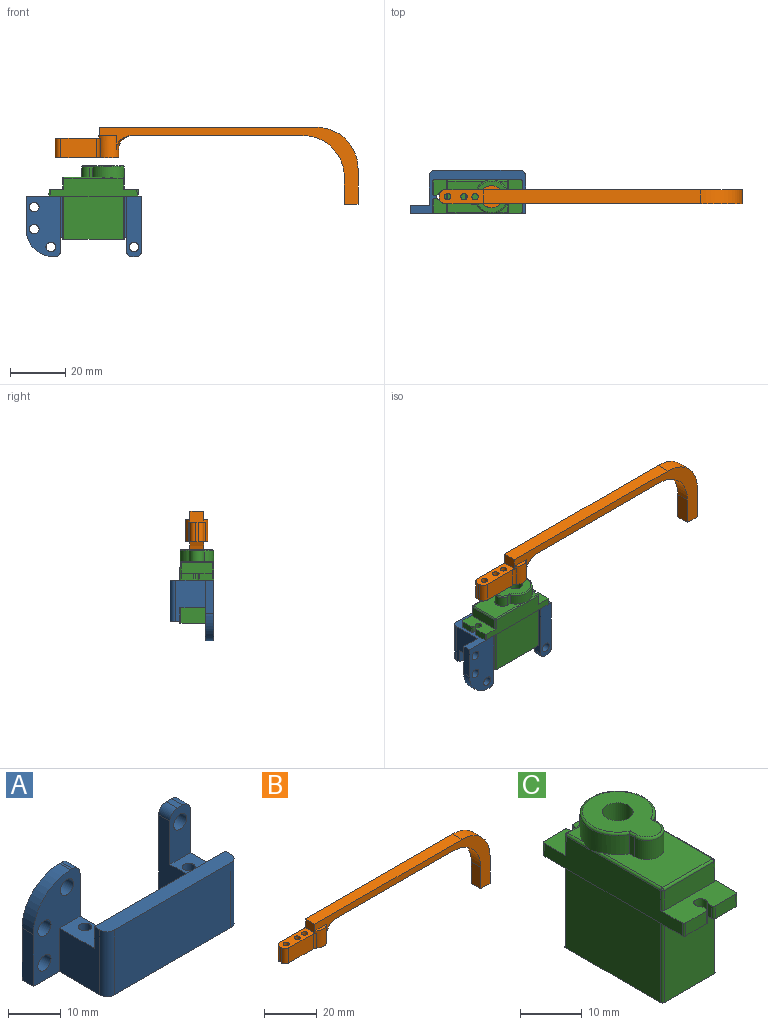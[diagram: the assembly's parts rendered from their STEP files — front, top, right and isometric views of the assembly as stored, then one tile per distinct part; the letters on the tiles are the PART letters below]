
ASSEMBLY  parts=3 mates=5
PART A: 29 faces, bbox 42x15.8x22 mm
  f0: plane 22x12.5mm, normal (0,1,0), area 223.8mm2, adj f1,f2,f5,f14,f15,f16,f17,f19
  f1: plane 42x15.8mm, normal (0,0,-1), area 267.3mm2, adj f0,f4,f5,f7,f9,f10,f11,f12
  f2: plane 3x0.5mm, normal (0,0,1), area 1.5mm2, adj f0,f13,f19,f23
  f3: plane 12x5.5mm, normal (0,-1,0), area 54.7mm2, adj f7,f8,f10,f18,f20,f22,f24
  f4: plane 15x10.8mm, normal (-1,0,0), area 115.5mm2, adj f1,f6,f12,f13,f21,f27
  f5: plane 20x12.3mm, normal (1,0,0), area 153mm2, adj f0,f1,f12,f13,f21,f23
  f6: plane 35x3.5mm, normal (0,0,1), area 120.8mm2, adj f4,f7,f11,f12,f27,f28
  f7: plane 20x13.8mm, normal (1,0,0), area 175.5mm2, adj f1,f3,f6,f9,f12,f20,f24,f28
  f8: plane 3x1.5mm, normal (0,0,1), area 4.5mm2, adj f3,f9,f22,f24
  f9: plane 22x5.5mm, normal (0,1,0), area 109.7mm2, adj f1,f7,f8,f10,f18,f22,f24
  f10: plane 20x12.3mm, normal (-1,0,0), area 153mm2, adj f1,f3,f9,f12,f20,f22
  f11: plane 31x15mm, normal (0,-1,0), area 465mm2, adj f1,f6,f27,f28
  f12: plane 35x15mm, normal (0,1,0), area 415mm2, adj f1,f4,f5,f6,f7,f10,f20,f21
  f13: plane 22x12.5mm, normal (0,-1,0), area 168.8mm2, adj f1,f2,f4,f5,f14,f15,f16,f17
  f14: plane 12x3mm, normal (-1,0,0), area 36mm2, adj f0,f1,f13,f19
  f15: cylinder r=1.75mm len=3.5mm, axis (0,-1,0), area 33mm2, adj f0,f13
  f16: cylinder r=1.75mm len=3.5mm, axis (0,-1,0), area 33mm2, adj f0,f13
  f17: cylinder r=1.75mm len=3.5mm, axis (0,-1,0), area 33mm2, adj f0,f13
  f18: cylinder r=1.75mm len=3.5mm, axis (0,-1,0), area 33mm2, adj f3,f9
  f19: cylinder r=10mm len=10mm, axis (0,-1,0), area 47.1mm2, adj f0,f2,f13,f14
  f20: plane 9.3x5.5mm, normal (0,0,1), area 46.2mm2, adj f3,f7,f10,f12,f26
  f21: plane 9.3x5.5mm, normal (0,0,1), area 46.2mm2, adj f4,f5,f12,f13,f25
  f22: cylinder r=2mm len=3mm, axis (0,-1,0), area 9.4mm2, adj f3,f8,f9,f10
  f23: cylinder r=2mm len=3mm, axis (0,1,0), area 9.4mm2, adj f0,f2,f5,f13
  f24: cylinder r=2mm len=3mm, axis (0,-1,0), area 9.4mm2, adj f3,f7,f8,f9
  f25: cylinder r=1.25mm len=10mm, axis (0,0,-1), area 78.5mm2, adj f1,f21
  f26: cylinder r=1.25mm len=10mm, axis (0,0,-1), area 78.5mm2, adj f1,f20
  f27: cylinder r=2mm len=15mm, axis (0,0,-1), area 47.1mm2, adj f1,f4,f6,f11
  f28: cylinder r=2mm len=15mm, axis (0,0,1), area 47.1mm2, adj f1,f6,f7,f11
PART B: 30 faces, bbox 110x12.2x28 mm
  f0: plane 7x1mm, normal (-1,0,0), area 7mm2, adj f15,f22,f28,f29
  f1: plane 13.03x7mm, normal (0,-1,0), area 91.2mm2, adj f15,f22,f26,f29
  f2: plane 94x28mm, normal (0,1,0), area 413.3mm2, adj f6,f7,f8,f9,f10,f13,f14,f20
  f3: cylinder r=1.15mm len=7mm, axis (0,0,-1), area 50.6mm2, adj f15,f22
  f4: cylinder r=1.15mm len=7mm, axis (0,0,-1), area 50.6mm2, adj f15,f22
  f5: cylinder r=1.15mm len=7mm, axis (0,0,-1), area 50.6mm2, adj f15,f22
  f6: plane 62.35x5mm, normal (0,0,-1), area 310.6mm2, adj f2,f11,f23,f25
  f7: plane 10x5mm, normal (-1,0,0), area 50mm2, adj f2,f8,f11,f23
  f8: plane 5x5mm, normal (0,0,-1), area 25mm2, adj f2,f7,f9,f11
  f9: plane 13x5mm, normal (1,0,0), area 65mm2, adj f2,f8,f11,f24
  f10: plane 79x5mm, normal (0,0,1), area 395mm2, adj f2,f11,f20,f24
  f11: plane 94x28mm, normal (0,-1,0), area 413.3mm2, adj f6,f7,f8,f9,f10,f14,f16,f20
  f12: plane 13.03x7mm, normal (0,1,0), area 91.2mm2, adj f15,f22,f27,f28
  f13: plane 6.25x1.5mm, normal (0,0,1), area 6.5mm2, adj f2,f14,f21
  f14: cylinder r=4mm len=8mm, axis (0,0,1), area 121.2mm2, adj f2,f11,f13,f15,f16,f19,f21,f22
  f15: plane 23x8mm, normal (0,0,-1), area 84.4mm2, adj f0,f1,f3,f4,f5,f12,f14,f17
  f16: plane 6.25x1.5mm, normal (0,0,1), area 6.5mm2, adj f11,f14,f19
  f17: cylinder r=3mm len=6mm, axis (0,0,-1), area 18.8mm2, adj f15,f18
  f18: plane 6x6mm, normal (0,0,-1), area 28.3mm2, adj f17
  f19: plane 1x0.12mm, normal (0,1,0), area 0.1mm2, adj f14,f16,f20,f22
  f20: plane 5x4mm, normal (-1,0,0), area 20mm2, adj f2,f10,f11,f19,f21,f22
  f21: plane 1x0.12mm, normal (0,-1,0), area 0.1mm2, adj f13,f14,f20,f22
  f22: plane 16.35x6mm, normal (0,0,1), area 66mm2, adj f0,f1,f3,f4,f5,f12,f14,f19
  f23: cylinder r=15mm len=15mm, axis (0,1,0), area 117.8mm2, adj f2,f6,f7,f11
  f24: cylinder r=15mm len=15mm, axis (0,1,0), area 117.8mm2, adj f2,f9,f10,f11
  f25: torus R=9mm, axis (0,0,1), area 41mm2, adj f2,f6,f11,f14
  f26: cylinder r=2mm len=7mm, axis (0,0,1), area 10.1mm2, adj f1,f14,f15,f22
  f27: cylinder r=2mm len=7mm, axis (0,0,1), area 10.1mm2, adj f12,f14,f15,f22
  f28: cylinder r=2mm len=7mm, axis (0,0,-1), area 22mm2, adj f0,f12,f15,f22
  f29: cylinder r=2mm len=7mm, axis (0,0,1), area 22mm2, adj f0,f1,f15,f22
PART C: 64 faces, bbox 13.2x32.4x26.7 mm
  f0: plane 3.52x3.52mm, normal (0,0,1), area 4.4mm2, adj f4,f7,f57
  f1: plane 3.52x3.52mm, normal (0,0,1), area 4.4mm2, adj f5,f8,f57
  f2: plane 13.72x11.39mm, normal (0,0,1), area 107.7mm2, adj f3,f6,f47,f53,f54,f57,f58
  f3: cylinder r=0.4mm len=15.89mm, axis (0,1,0), area 9.3mm2, adj f2,f17,f45,f57
  f4: cylinder r=0.4mm len=5.69mm, axis (0,1,0), area 2.9mm2, adj f0,f17,f50,f57
  f5: cylinder r=0.4mm len=5.69mm, axis (0,1,0), area 2.9mm2, adj f1,f15,f51,f57
  f6: cylinder r=0.4mm len=15.89mm, axis (0,1,0), area 9.3mm2, adj f2,f15,f49,f57
  f7: cylinder r=0.4mm len=5.69mm, axis (-1,0,0), area 2.9mm2, adj f0,f16,f50,f57
  f8: cylinder r=0.4mm len=5.69mm, axis (-1,0,0), area 2.9mm2, adj f1,f16,f51,f57
  f9: plane 4.73x2.5mm, normal (0,1,0.01), area 11.8mm2, adj f11,f12,f32,f36
  f10: plane 4.73x2.5mm, normal (0,1,0.01), area 11.8mm2, adj f11,f12,f33,f37
  f11: plane 12.3x5.35mm, normal (0,0,-1), area 55.4mm2, adj f9,f10,f15,f17,f22,f29,f30,f31
  f12: plane 12.26x5.35mm, normal (0,0,1), area 55.2mm2, adj f9,f10,f15,f16,f17,f29,f30,f31
  f13: plane 4.73x2.5mm, normal (0,-1,0.01), area 11.8mm2, adj f14,f25,f34,f38
  f14: plane 12.26x5.35mm, normal (0,0,1), area 55.2mm2, adj f13,f15,f17,f18,f24,f26,f27,f28
  f15: plane 31.6x6.4mm, normal (1,0,0.01), area 163.4mm2, adj f5,f6,f11,f12,f14,f23,f25,f36
  f16: plane 11.46x3.9mm, normal (0,1,0.01), area 44.6mm2, adj f7,f8,f12,f48,f52
  f17: plane 31.6x6.4mm, normal (-1,0,0.01), area 163.4mm2, adj f3,f4,f11,f12,f14,f21,f25,f37
  f18: plane 11.46x3.9mm, normal (0,-1,0.01), area 44.6mm2, adj f14,f44,f46,f47
  f19: plane 22.5x12.3mm, normal (0,0,-1), area 276.6mm2, adj f20,f21,f22,f23,f40,f41,f42,f43
  f20: plane 15.7x11.5mm, normal (0,-1,0), area 180.5mm2, adj f19,f25,f42,f43
  f21: plane 21.7x15.7mm, normal (-1,0,0), area 340.7mm2, adj f17,f19,f41,f42
  f22: plane 15.7x11.5mm, normal (0,1,0), area 180.5mm2, adj f11,f19,f40,f41
  f23: plane 21.7x15.7mm, normal (1,0,0), area 340.7mm2, adj f15,f19,f40,f43
  f24: plane 4.73x2.5mm, normal (0,-1,0.01), area 11.8mm2, adj f14,f25,f35,f39
  f25: plane 12.3x5.35mm, normal (0,0,-1), area 55.4mm2, adj f13,f15,f17,f20,f24,f26,f27,f28
  f26: cylinder r=1.1mm len=2.5mm, axis (0,0,1), area 14mm2, adj f14,f25,f27,f28
  f27: plane 2.5x1.04mm, normal (1,0,0), area 2.6mm2, adj f14,f25,f26,f34
  f28: plane 2.5x1.04mm, normal (-1,0,0), area 2.6mm2, adj f14,f25,f26,f35
  f29: plane 2.5x1.04mm, normal (-1,0,0), area 2.6mm2, adj f11,f12,f31,f32
  f30: plane 2.5x1.04mm, normal (1,0,0), area 2.6mm2, adj f11,f12,f31,f33
  f31: cylinder r=1.1mm len=2.5mm, axis (0,0,1), area 14mm2, adj f11,f12,f29,f30
  f32: cylinder r=0.4mm len=2.51mm, axis (0,0.01,-1), area 1.6mm2, adj f9,f11,f12,f29
  f33: cylinder r=0.4mm len=2.51mm, axis (0,-0.01,1), area 1.6mm2, adj f10,f11,f12,f30
  f34: cylinder r=0.4mm len=2.51mm, axis (0,0.01,1), area 1.6mm2, adj f13,f14,f25,f27
  f35: cylinder r=0.4mm len=2.51mm, axis (0,-0.01,-1), area 1.6mm2, adj f14,f24,f25,f28
  f36: cylinder r=0.4mm len=2.5mm, axis (0.01,0.01,-1), area 1.6mm2, adj f9,f11,f12,f15
  f37: cylinder r=0.4mm len=2.5mm, axis (-0.01,0.01,-1), area 1.6mm2, adj f10,f11,f12,f17
  f38: cylinder r=0.4mm len=2.5mm, axis (-0.01,-0.01,-1), area 1.6mm2, adj f13,f14,f17,f25
  f39: cylinder r=0.4mm len=2.5mm, axis (0.01,-0.01,-1), area 1.6mm2, adj f14,f15,f24,f25
  f40: cylinder r=0.4mm len=15.7mm, axis (0,0,-1), area 9.9mm2, adj f11,f19,f22,f23
  f41: cylinder r=0.4mm len=15.7mm, axis (0,0,1), area 9.9mm2, adj f11,f19,f21,f22
  f42: cylinder r=0.4mm len=15.7mm, axis (0,0,-1), area 9.9mm2, adj f19,f20,f21,f25
  f43: cylinder r=0.4mm len=15.7mm, axis (0,0,1), area 9.9mm2, adj f19,f20,f23,f25
  f44: cylinder r=0.4mm len=3.91mm, axis (-0.01,-0.01,-1), area 2.5mm2, adj f14,f17,f18,f45
  f45: sphere r=0.4mm, area 0.2mm2, adj f3,f44,f47
  f46: cylinder r=0.4mm len=3.91mm, axis (0.01,-0.01,-1), area 2.5mm2, adj f14,f15,f18,f49
  f47: cylinder r=0.4mm len=11.39mm, axis (-1,0,0), area 7.1mm2, adj f2,f18,f45,f49
  f48: cylinder r=0.4mm len=3.91mm, axis (-0.01,0.01,-1), area 2.5mm2, adj f12,f16,f17,f50
  f49: sphere r=0.4mm, area 0.2mm2, adj f6,f46,f47
  f50: sphere r=0.4mm, area 0.2mm2, adj f4,f7,f48
  f51: sphere r=0.4mm, area 0.2mm2, adj f5,f8,f52
  f52: cylinder r=0.4mm len=3.91mm, axis (0.01,0.01,-1), area 2.5mm2, adj f12,f15,f16,f51
  f53: plane 3.8x1.22mm, normal (-1,0,0), area 4.6mm2, adj f2,f54,f57,f61
  f54: cylinder r=2.75mm len=5.5mm, axis (0,0,-1), area 32.8mm2, adj f2,f53,f58,f63
  f55: plane 14.7x11.39mm, normal (0,0,1), area 96.2mm2, adj f56,f60,f61,f62,f63
  f56: cylinder r=2.5mm len=5mm, axis (0,0,-1), area 66mm2, adj f55,f59
  f57: cylinder r=6.09mm len=12.19mm, axis (0,0,-1), area 125.9mm2, adj f0,f1,f2,f3,f4,f5,f6,f7
  f58: plane 3.8x1.22mm, normal (1,0,0), area 4.6mm2, adj f2,f54,f57,f62
  f59: plane 5x5mm, normal (0,0,1), area 19.6mm2, adj f56
  f60: torus R=5.69mm, axis (0,0,1), area 20.1mm2, adj f55,f57,f61,f62
  f61: cylinder r=0.4mm len=1.47mm, axis (0,1,0), area 0.8mm2, adj f53,f55,f60,f63
  f62: cylinder r=0.4mm len=1.47mm, axis (0,-1,0), area 0.8mm2, adj f55,f58,f60,f63
  f63: torus R=2.35mm, axis (0,0,1), area 5.1mm2, adj f54,f55,f61,f62
PLACE A rot(axis=(-1,0,0),180deg) t=(29.31,-50.95,-55.05)mm
PLACE B t=(15.46,-52.3,-71.58)mm
PLACE C rot(axis=(0,0,-1),90deg) t=(29.36,-54.8,-55.05)mm
MATE planar C.f55 <-> B.f14  axis (0,0,1) through (29.27,-52.45,-44.05)mm
MATE cylindrical C.f56 <-> B.f14  axis (0,0,1) through (34.46,-54.8,-44.05)mm
MATE cylindrical A.f26 <-> C.f31  axis (0,0,1) through (43.21,-54.8,-55.05)mm
MATE planar A.f1 <-> C.f11  axis (0,0,1) through (44.06,-60.95,-55.05)mm
MATE planar C.f23 <-> A.f0  axis (0,-1,0) through (29.36,-60.95,-62.9)mm
